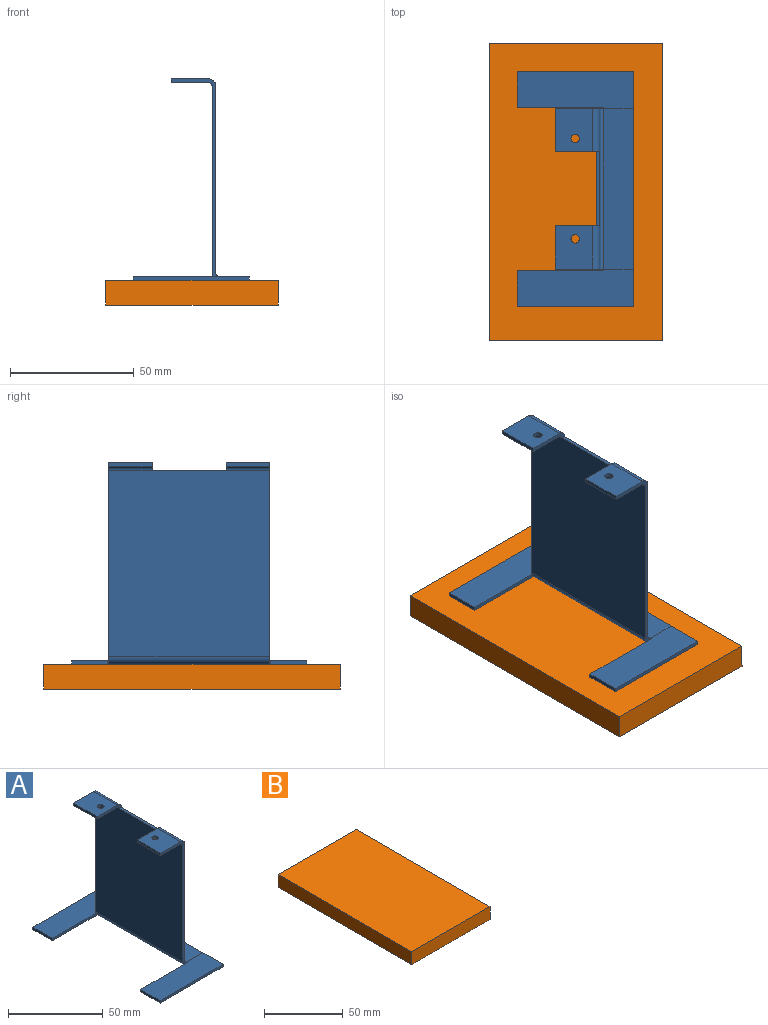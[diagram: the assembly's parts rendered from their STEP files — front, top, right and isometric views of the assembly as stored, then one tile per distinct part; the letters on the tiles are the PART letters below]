
ASSEMBLY  parts=2 mates=1
PART A: 34 faces, bbox 47x95x81.5 mm
  f0: plane 65x12mm, normal (0,0,1), area 780mm2, adj f1,f7,f11,f26
  f1: plane 47x15mm, normal (0,0,1), area 687.5mm2, adj f0,f2,f4,f5,f7,f32
  f2: plane 1.5x0.5mm, normal (-1,0,0), area 0.7mm2, adj f1,f3,f4,f6
  f3: plane 81.5x19.5mm, normal (0,-1,0), area 146.4mm2, adj f2,f23,f25,f26,f27,f28,f29,f30
  f4: plane 35x1.5mm, normal (0,1,0), area 52.5mm2, adj f1,f2,f5,f6
  f5: plane 14.5x1.5mm, normal (-1,0,0), area 21.7mm2, adj f1,f4,f6,f32
  f6: plane 95x47mm, normal (0,0,-1), area 2155mm2, adj f2,f4,f5,f7,f8,f9,f10,f12
  f7: plane 95x1.5mm, normal (1,0,0), area 142.5mm2, adj f0,f1,f6,f10,f11,f32
  f8: plane 14.5x1.5mm, normal (-1,0,0), area 21.7mm2, adj f6,f9,f10,f11
  f9: plane 35x1.5mm, normal (0,-1,0), area 52.5mm2, adj f6,f8,f11,f12
  f10: plane 47x1.5mm, normal (0,1,0), area 70.5mm2, adj f6,f7,f8,f11
  f11: plane 47x15mm, normal (0,0,1), area 687.5mm2, adj f0,f7,f8,f9,f10,f12
  f12: plane 1.5x0.5mm, normal (-1,0,0), area 0.7mm2, adj f6,f9,f11,f16
  f13: cylinder r=1.7mm len=3.4mm, axis (0,0,-1), area 16mm2, adj f15,f18
  f14: plane 17.5x1.5mm, normal (-1,0,0), area 26.2mm2, adj f15,f16,f17,f18
  f15: plane 17.5x15mm, normal (0,0,-1), area 253.4mm2, adj f13,f14,f16,f17,f19
  f16: plane 81.5x19.5mm, normal (0,1,0), area 146.4mm2, adj f12,f14,f15,f18,f19,f24,f25,f26
  f17: plane 18x3mm, normal (0,-1,0), area 27.8mm2, adj f14,f15,f18,f19,f20,f24
  f18: plane 17.5x15mm, normal (0,0,1), area 253.4mm2, adj f13,f14,f16,f17,f24
  f19: cylinder r=1.5mm len=17.5mm, axis (0,1,0), area 41.2mm2, adj f15,f16,f17,f27
  f20: plane 30x1.5mm, normal (0,0,1), area 45mm2, adj f17,f22,f25,f27
  f21: cylinder r=1.7mm len=3.4mm, axis (0,0,-1), area 16mm2, adj f23,f29
  f22: plane 18x3mm, normal (0,1,0), area 27.8mm2, adj f20,f23,f28,f29,f30,f33
  f23: plane 17.5x15mm, normal (0,0,1), area 253.4mm2, adj f3,f21,f22,f30,f33
  f24: cylinder r=3mm len=17.5mm, axis (0,-1,0), area 82.5mm2, adj f16,f17,f18,f25
  f25: plane 75.5x65mm, normal (1,0,0), area 4907.5mm2, adj f3,f16,f20,f24,f26,f33
  f26: cylinder r=1.5mm len=65mm, axis (0,-1,0), area 153.2mm2, adj f0,f3,f16,f25
  f27: plane 75.5x65mm, normal (-1,0,0), area 4907.5mm2, adj f3,f16,f19,f20,f28,f31
  f28: cylinder r=1.5mm len=17.5mm, axis (0,-1,0), area 41.2mm2, adj f3,f22,f27,f29
  f29: plane 17.5x15mm, normal (0,0,-1), area 253.4mm2, adj f3,f21,f22,f28,f30
  f30: plane 17.5x1.5mm, normal (-1,0,0), area 26.3mm2, adj f3,f22,f23,f29
  f31: cylinder r=3mm len=65mm, axis (0,-1,0), area 306.3mm2, adj f3,f6,f16,f27
  f32: plane 47x1.5mm, normal (0,-1,0), area 70.5mm2, adj f1,f5,f6,f7
  f33: cylinder r=3mm len=17.5mm, axis (0,-1,0), area 82.5mm2, adj f3,f22,f23,f25
PART B: 6 faces, bbox 70x120x10 mm
  f0: plane 120x10mm, normal (-1,0,0), area 1200mm2, adj f1,f3,f4,f5
  f1: plane 70x10mm, normal (0,1,0), area 700mm2, adj f0,f2,f4,f5
  f2: plane 120x10mm, normal (1,0,0), area 1200mm2, adj f1,f3,f4,f5
  f3: plane 70x10mm, normal (0,-1,0), area 700mm2, adj f0,f2,f4,f5
  f4: plane 120x70mm, normal (0,0,-1), area 8400mm2, adj f0,f1,f2,f3
  f5: plane 120x70mm, normal (0,0,1), area 8400mm2, adj f0,f1,f2,f3
PLACE A t=(-20.78,4.92,15.62)mm
PLACE B rot(axis=(-0.71,0.71,0),0deg) t=(-19.86,6.07,15.62)mm
MATE planar B.f5 <-> A.f6  axis (0,0,1) through (-23.53,-11.49,25.62)mm
